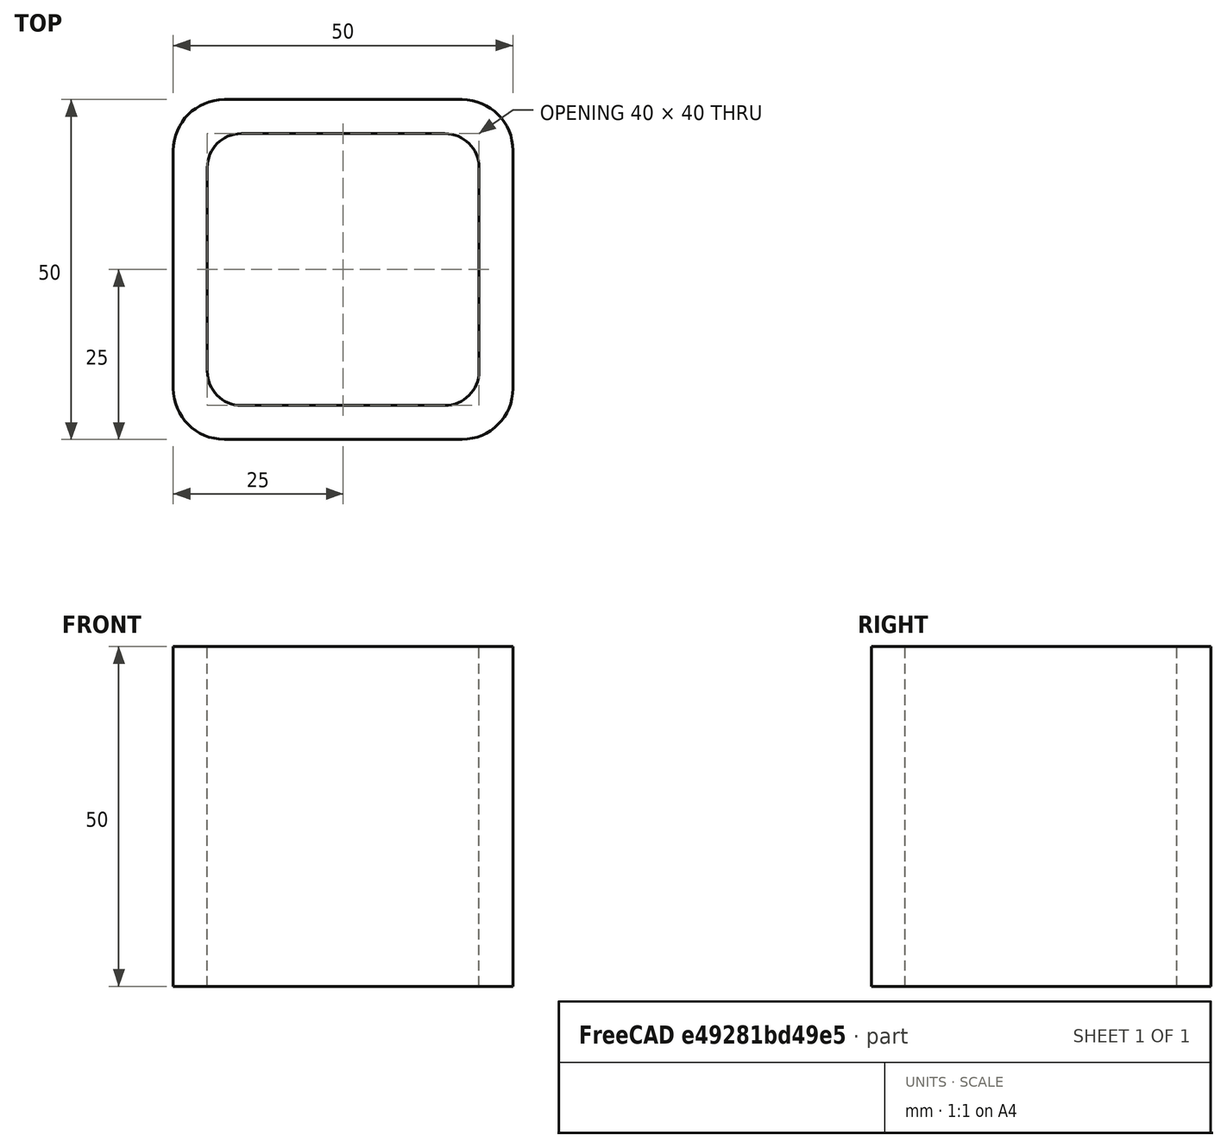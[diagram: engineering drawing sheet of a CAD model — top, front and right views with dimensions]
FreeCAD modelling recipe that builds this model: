
FCSTD DOCUMENT  (FreeCAD 0.15R4671 (Git))
Label: Square hollow section 50x50x5 EN10219 S235JRH
License: All rights reserved
LicenseURL: http://en.wikipedia.org/wiki/All_rights_reserved
objects: Sketcher::SketchObject×1, Part::Extrusion×1
note: 2 computed .brp shape members not serialized (recipe doc carries the construction recipe); baked Part::Feature solids carry a one-line shape summary decoded from their .brp

FEATURE [Sketcher::SketchObject] Sketch
  sketch-geometry (16):
    g0: LineSegment StartX=-15 StartY=20 StartZ=0 EndX=15 EndY=20 EndZ=0
    g1: LineSegment StartX=20 StartY=15 StartZ=0 EndX=20 EndY=-15 EndZ=0
    g2: LineSegment StartX=15 StartY=-20 StartZ=0 EndX=-15 EndY=-20 EndZ=0
    g3: LineSegment StartX=-20 StartY=-15 StartZ=0 EndX=-20 EndY=15 EndZ=0
    g4: LineSegment StartX=-17.5 StartY=25 StartZ=0 EndX=17.5 EndY=25 EndZ=0
    g5: LineSegment StartX=25 StartY=17.5 StartZ=0 EndX=25 EndY=-17.5 EndZ=0
    g6: LineSegment StartX=17.5 StartY=-25 StartZ=0 EndX=-17.5 EndY=-25 EndZ=0
    g7: LineSegment StartX=-25 StartY=-17.5 StartZ=0 EndX=-25 EndY=17.5 EndZ=0
    g8: ArcOfCircle CenterX=-15 CenterY=15 CenterZ=0 NormalX=0 NormalY=0 NormalZ=1 Radius=5 StartAngle=1.5708 EndAngle=3.14159
    g9: ArcOfCircle CenterX=15 CenterY=15 CenterZ=0 NormalX=0 NormalY=0 NormalZ=1 Radius=5 StartAngle=0 EndAngle=1.5708
    g10: ArcOfCircle CenterX=15 CenterY=-15 CenterZ=0 NormalX=0 NormalY=0 NormalZ=1 Radius=5 StartAngle=4.71239 EndAngle=6.28319
    g11: ArcOfCircle CenterX=-15 CenterY=-15 CenterZ=0 NormalX=0 NormalY=0 NormalZ=1 Radius=5 StartAngle=3.14159 EndAngle=4.71239
    g12: ArcOfCircle CenterX=17.5 CenterY=17.5 CenterZ=0 NormalX=0 NormalY=0 NormalZ=1 Radius=7.5 StartAngle=0 EndAngle=1.5708
    g13: ArcOfCircle CenterX=17.5 CenterY=-17.5 CenterZ=0 NormalX=0 NormalY=0 NormalZ=1 Radius=7.5 StartAngle=4.71239 EndAngle=6.28319
    g14: ArcOfCircle CenterX=-17.5 CenterY=-17.5 CenterZ=0 NormalX=0 NormalY=0 NormalZ=1 Radius=7.5 StartAngle=3.14159 EndAngle=4.71239
    g15: ArcOfCircle CenterX=-17.5 CenterY=17.5 CenterZ=0 NormalX=0 NormalY=0 NormalZ=1 Radius=7.5 StartAngle=1.5708 EndAngle=3.14159
  constraints (36):
    c: Horizontal(g2)
    c: Vertical(g3)
    c: Horizontal(g6)
    c: Vertical(g7)
    c: Tangent(g3,g8) = 1.5708
    c: Tangent(g0,g8) = 1.5708
    c: Tangent(g0,g9) = 1.5708
    c: Tangent(g1,g9) = 1.5708
    c: Tangent(g1,g10) = 1.5708
    c: Tangent(g2,g10) = 1.5708
    c: Tangent(g2,g11) = 1.5708
    c: Tangent(g3,g11) = 1.5708
    c: Tangent(g4,g12) = 1.5708
    c: Tangent(g5,g12) = 1.5708
    c: Tangent(g5,g13) = 1.5708
    c: Tangent(g6,g13) = 1.5708
    c: Tangent(g6,g14) = 1.5708
    c: Tangent(g7,g14) = 1.5708
    c: Tangent(g7,g15) = 1.5708
    c: Tangent(g4,g15) = 1.5708
    c: Equal(g9,g8)
    c: Equal(g9,g11)
    c: Equal(g9,g10)
    c: Equal(g12,g15)
    c: Equal(g12,g14)
    c: Equal(g12,g13)
    c: Symmetric(g4,g6,g-1)
    c: Symmetric(g7,g5,g-2)
    c: DistanceY(g4,g6) = -50
    c: DistanceX(g7,g5) = 50
    c: Symmetric(g3,g1,g-2)
    c: Symmetric(g0,g2,g-1)
    c: DistanceY(g0,g4) = 5
    c: DistanceX(g5,g1) = -5
    c: Radius(g9) = 5
    c: Radius(g12) = 7.5
FEATURE [Part::Extrusion] Extrude  label="Square hollow section 50x50x5 EN10219 S235JRH"
  Base = -> Sketch
  Dir = (0,0,50)
  Solid = true
